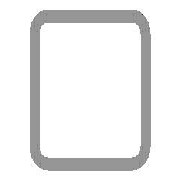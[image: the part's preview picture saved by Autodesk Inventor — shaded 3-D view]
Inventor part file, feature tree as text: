
AUTODESK INVENTOR PART (.ipt)
format: ipt  version: 2025.1 (Build 291241020, 241B)  size: 134,656 bytes
history: native  units: mm (DEFAULTED — no unit token found)
features: other x4, sketch x1, plane x1
ambient origin geometry x8: Origin, YZ Plane, XZ Plane, XY Plane, X Axis, Y Axis, Z Axis, Center Point
bodies: Solid1 (feature_tree), Body (feature_tree)
feature tree (6):
  parser-record x1  (decoder bookkeeping rows leaked as tree rows — omitted from the tree; the rows remain in map.json)
  other  "Driven Length"
  other  "Start Plane"
  other  "End Plane"
  sketch  "Sketch3"  dims[d3=1050.0mm d4=0.0mm d7=4.0mm d9=40.0mm d11=40.0mm d12=2.0mm d13=50.0mm d14=1100.0mm d15=20.0mm d16=20.0mm d17=90.0deg d18=1050.0mm]
  plane  "Work Plane3"
